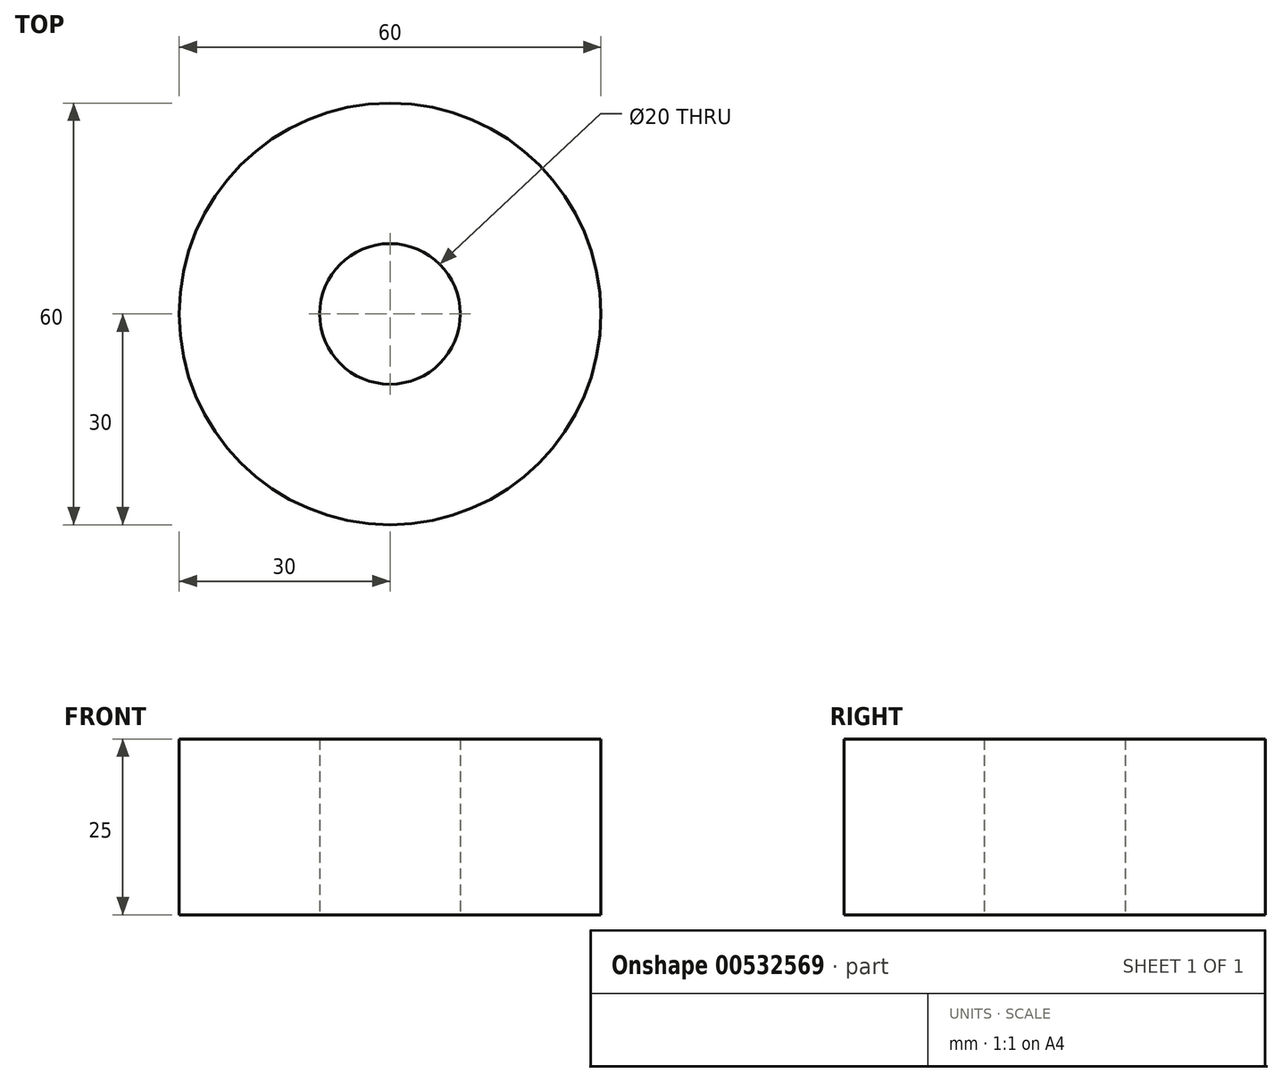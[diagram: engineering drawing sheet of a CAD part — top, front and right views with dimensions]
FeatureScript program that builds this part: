
annotation { "Feature Type Name" : "Feature", "Feature Type Description" : "" }
export const myFeature = defineFeature(function(context is Context, id is Id, definition is map)
    precondition{}
    {
        {
            var Q0;
            Q0=qCreatedBy(makeId("Top.planeOp"),FACE);
            var sketch = newSketch(context, id + "F0", { "sketchPlane" : qUnion([Q0])});
            skCircle(sketch, "E0", {"center": v(0, 0) * mm, "radius": 30 * mm});
            skCircle(sketch, "E1", {"center": v(0, 0) * mm, "radius": 10 * mm});
            skSolve(sketch);
        }
        {
            var Q0;
            Q0=makeQuery(id+"F0.imprint","IMPRINT",FACE,{"disambiguationData":[TD([[makeQuery(id+"F0.imprint","IMPRINT",EDGE,{"derivedFrom":sQuery(id+"F0.wireOp",EDGE,"E0")}),1.0]])]});
            extrude(context, id + "F1", {"entities" : qUnion([Q0]), "depth" : 25 * mm, "offsetDistance" : 25 * mm});
        }
    });
